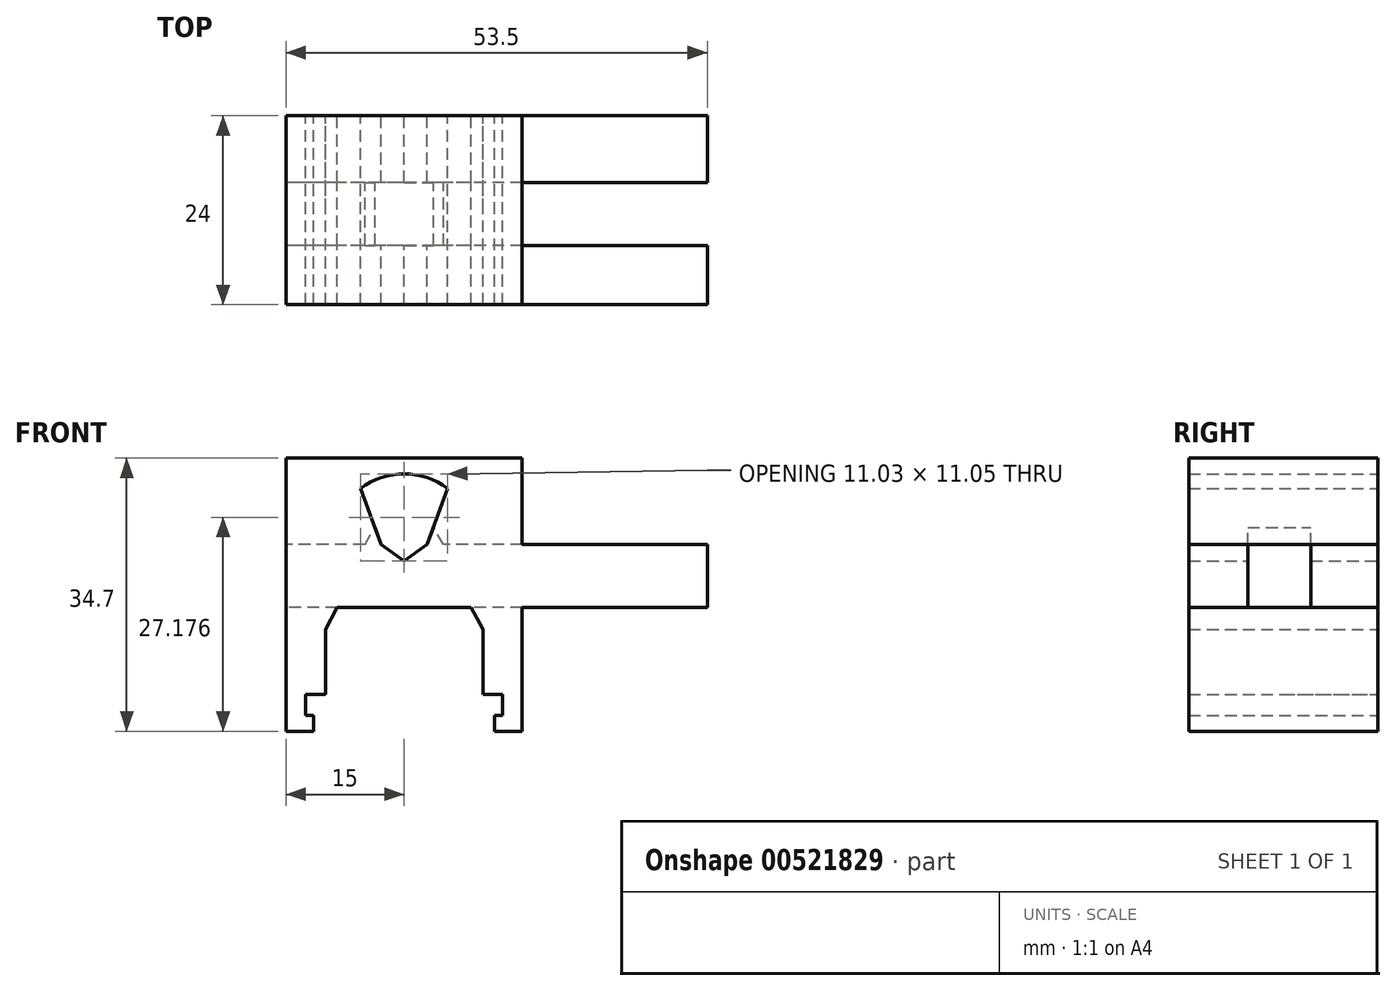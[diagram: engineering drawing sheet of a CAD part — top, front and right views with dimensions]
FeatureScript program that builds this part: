
annotation { "Feature Type Name" : "Feature", "Feature Type Description" : "" }
export const myFeature = defineFeature(function(context is Context, id is Id, definition is map)
    precondition{}
    {
        {
            var Q0;
            Q0=qCreatedBy(makeId("Front.planeOp"),FACE);
            var sketch = newSketch(context, id + "F0", { "sketchPlane" : qUnion([Q0])});
            skLineSegment(sketch, "E0.bottom", {"start": v(15, 15) * mm, "end": v(-15, 15) * mm});
            skLineSegment(sketch, "E0.top", {"start": v(15, -15) * mm, "end": v(-15, -15) * mm});
            skLineSegment(sketch, "E0.left", {"start": v(15, 15) * mm, "end": v(15, -15) * mm});
            skLineSegment(sketch, "E0.right", {"start": v(-15, 15) * mm, "end": v(-15, -15) * mm});
            skLineSegment(sketch, "E1", {"start": v(0, 0) * mm, "end": v(0, -17.35) * mm});
            skLineSegment(sketch, "E2.top", {"start": v(15, -19.7) * mm, "end": v(-15, -19.7) * mm});
            skLineSegment(sketch, "E2.left", {"start": v(15, -15) * mm, "end": v(15, -19.7) * mm});
            skLineSegment(sketch, "E2.right", {"start": v(-15, -15) * mm, "end": v(-15, -19.7) * mm});
            skPoint(sketch, "E2.middle", {"position": v(0, -17.35) * mm});
            skLineSegment(sketch, "E3.0", {"start": v(15, -17.7) * mm, "end": v(-15, -17.7) * mm});
            skLineSegment(sketch, "E4.0", {"start": v(-12.5, -15) * mm, "end": v(-12.5, -17.7) * mm});
            skLineSegment(sketch, "E5.0", {"start": v(12.5, -15) * mm, "end": v(12.5, -17.7) * mm});
            skLineSegment(sketch, "E6.0", {"start": v(-11.5, -17.7) * mm, "end": v(-11.5, -20) * mm});
            skLineSegment(sketch, "E7.0", {"start": v(11.5, -17.7) * mm, "end": v(11.5, -20) * mm});
            skCircle(sketch, "E8", {"center": v(0, 30) * mm, "radius": 2 * mm});
            skLineSegment(sketch, "E9", {"start": v(0, 30) * mm, "end": v(-5.14, 36.13) * mm});
            skPoint(sketch, "E9.endSnap0", {"position": v(0, 15) * mm});
            skLineSegment(sketch, "E10", {"start": v(0, 30) * mm, "end": v(9.64, 18.5) * mm});
            skLineSegment(sketch, "E11", {"start": v(0, 30) * mm, "end": v(-2.3, 28.07) * mm});
            skLineSegment(sketch, "E12", {"start": v(0, 30) * mm, "end": v(2.3, 31.93) * mm});
            skLineSegment(sketch, "E13", {"start": v(2.3, 31.93) * mm, "end": v(-5.14, 36.13) * mm});
            skLineSegment(sketch, "E14", {"start": v(-5.14, 36.13) * mm, "end": v(-2.3, 28.07) * mm});
            skLineSegment(sketch, "E15", {"start": v(9.64, 18.5) * mm, "end": v(-2.3, 28.07) * mm});
            skLineSegment(sketch, "E16", {"start": v(9.64, 18.5) * mm, "end": v(2.3, 31.93) * mm});
            skLineSegment(sketch, "E17", {"start": v(0, -15) * mm, "end": v(-10, -15) * mm});
            skLineSegment(sketch, "E18", {"start": v(0, -15) * mm, "end": v(10, -15) * mm});
            skLineSegment(sketch, "E19.bottom", {"start": v(8.5, 4) * mm, "end": v(-38.5, 4) * mm});
            skLineSegment(sketch, "E19.top", {"start": v(8.5, -4) * mm, "end": v(-38.5, -4) * mm});
            skLineSegment(sketch, "E19.left", {"start": v(8.5, 4) * mm, "end": v(8.5, -4) * mm});
            skLineSegment(sketch, "E19.right", {"start": v(-38.5, 4) * mm, "end": v(-38.5, -4) * mm});
            skPoint(sketch, "E19.middle", {"position": v(-15, 0) * mm});
            skLineSegment(sketch, "E20.bottom", {"start": v(38.5, 4) * mm, "end": v(-8.5, 4) * mm});
            skLineSegment(sketch, "E20.top", {"start": v(38.5, -4) * mm, "end": v(-8.5, -4) * mm});
            skLineSegment(sketch, "E20.left", {"start": v(38.5, 4) * mm, "end": v(38.5, -4) * mm});
            skLineSegment(sketch, "E20.right", {"start": v(-8.5, 4) * mm, "end": v(-8.5, -4) * mm});
            skPoint(sketch, "E20.middle", {"position": v(15, 0) * mm});
            skLineSegment(sketch, "E21", {"start": v(8.5, -4) * mm, "end": v(-2.93, 4) * mm});
            skLineSegment(sketch, "E22", {"start": v(-8.5, -4) * mm, "end": v(2.93, 4) * mm});
            skLineSegment(sketch, "E23", {"start": v(0, 0) * mm, "end": v(0, 45) * mm});
            skLineSegment(sketch, "E24", {"start": v(0, 0) * mm, "end": v(0, 30) * mm});
            skLineSegment(sketch, "E25.0", {"start": v(10, 15) * mm, "end": v(10, -15) * mm});
            skLineSegment(sketch, "E26.0", {"start": v(-10, 15.04) * mm, "end": v(-10, -15) * mm});
            skArc(sketch, "E27", {"start": v(5.51, 11.11) * mm, "mid": v(0, 13) * mm, "end": v(-5.51, 11.11) * mm});
            skLineSegment(sketch, "E28", {"start": v(2.93, 4) * mm, "end": v(5.51, 11.11) * mm});
            skLineSegment(sketch, "E29", {"start": v(-2.93, 4) * mm, "end": v(-5.51, 11.11) * mm});
            skLineSegment(sketch, "E30", {"start": v(8.5, -4) * mm, "end": v(10, -6.74) * mm});
            skLineSegment(sketch, "E31", {"start": v(-8.5, -4) * mm, "end": v(-10, -6.74) * mm});
            skLineSegment(sketch, "E32", {"start": v(5, 4) * mm, "end": v(3.73, 6.2) * mm});
            skLineSegment(sketch, "E33", {"start": v(-5, 4) * mm, "end": v(-3.73, 6.2) * mm});
            skSolve(sketch);
        }
        {
            var Q0;
            {var subQ0=sQuery(id+"F0.wireOp",EDGE,"E19.bottom");var subQ1=sQuery(id+"F0.wireOp",EDGE,"E0.right");var subQ2=makeQuery(id+"F0.imprint","INTERSECT",VERTEX,{"derivedFrom":[subQ1,subQ0]});Q0=makeQuery(id+"F0.imprint","IMPRINT",FACE,{"disambiguationData":[TD([[makeQuery(id+"F0.imprint","IMPRINT",EDGE,{"disambiguationData":[TD([[subQ2,-1.0]])],"derivedFrom":subQ1}),1.0]])]});}
            var Q1;
            {var subQ0=sQuery(id+"F0.wireOp",EDGE,"E0.left");var subQ1=sQuery(id+"F0.wireOp",EDGE,"E0.bottom");var subQ2=makeQuery(id+"F0.imprint","INTERSECT",VERTEX,{"derivedFrom":[subQ1,subQ0]});Q1=makeQuery(id+"F0.imprint","IMPRINT",FACE,{"disambiguationData":[TD([[makeQuery(id+"F0.imprint","IMPRINT",EDGE,{"disambiguationData":[TD([[subQ2,-1.0]])],"derivedFrom":subQ1}),1.0]])]});}
            var Q2;
            {var subQ7=sQuery(id+"F0.wireOp",EDGE,"E32");Q2=makeQuery(id+"F0.imprint","IMPRINT",FACE,{"disambiguationData":[TD([[makeQuery(id+"F0.imprint","IMPRINT",EDGE,{"derivedFrom":subQ7}),-1.0]])]});}
            var Q3;
            {var subQ0=sQuery(id+"F0.wireOp",EDGE,"E24");var subQ1=sQuery(id+"F0.wireOp",EDGE,"E1");var subQ2=makeQuery(id+"F0.imprint","INTERSECT",VERTEX,{"derivedFrom":[subQ1,subQ0]});Q3=makeQuery(id+"F0.imprint","IMPRINT",FACE,{"disambiguationData":[TD([[makeQuery(id+"F0.imprint","IMPRINT",EDGE,{"disambiguationData":[TD([[subQ2,-1.0]])],"derivedFrom":subQ1}),-1.0]])]});}
            var Q4;
            {var subQ4=sQuery(id+"F0.wireOp",EDGE,"E2.left");var subQ6=sQuery(id+"F0.wireOp",EDGE,"E2.top");var subQ7=makeQuery(id+"F0.imprint","INTERSECT",VERTEX,{"derivedFrom":[subQ6,subQ4]});Q4=makeQuery(id+"F0.imprint","IMPRINT",FACE,{"disambiguationData":[TD([[makeQuery(id+"F0.imprint","IMPRINT",EDGE,{"disambiguationData":[TD([[subQ7,-1.0]])],"derivedFrom":subQ6}),-1.0]])]});}
            var Q5;
            {var subQ0=sQuery(id+"F0.wireOp",EDGE,"E24");var subQ1=sQuery(id+"F0.wireOp",EDGE,"E1");var subQ2=makeQuery(id+"F0.imprint","INTERSECT",VERTEX,{"derivedFrom":[subQ1,subQ0]});Q5=makeQuery(id+"F0.imprint","IMPRINT",FACE,{"disambiguationData":[TD([[makeQuery(id+"F0.imprint","IMPRINT",EDGE,{"disambiguationData":[TD([[subQ2,-1.0]])],"derivedFrom":subQ1}),1.0]])]});}
            var Q6;
            {var subQ0=sQuery(id+"F0.wireOp",EDGE,"E30");Q6=makeQuery(id+"F0.imprint","IMPRINT",FACE,{"disambiguationData":[TD([[makeQuery(id+"F0.imprint","IMPRINT",EDGE,{"derivedFrom":subQ0}),1.0]])]});}
            var Q7;
            {var subQ3=sQuery(id+"F0.wireOp",EDGE,"E33");Q7=makeQuery(id+"F0.imprint","IMPRINT",FACE,{"disambiguationData":[TD([[makeQuery(id+"F0.imprint","IMPRINT",EDGE,{"derivedFrom":subQ3}),1.0]])]});}
            var Q8;
            {var subQ3=sQuery(id+"F0.wireOp",EDGE,"E5.0");Q8=makeQuery(id+"F0.imprint","IMPRINT",FACE,{"disambiguationData":[TD([[makeQuery(id+"F0.imprint","IMPRINT",EDGE,{"derivedFrom":subQ3}),1.0]])]});}
            var Q9;
            {var subQ5=sQuery(id+"F0.wireOp",EDGE,"E18");Q9=makeQuery(id+"F0.imprint","IMPRINT",FACE,{"disambiguationData":[TD([[makeQuery(id+"F0.imprint","IMPRINT",EDGE,{"derivedFrom":subQ5}),1.0]])]});}
            var Q10;
            {var subQ4=sQuery(id+"F0.wireOp",EDGE,"E20.top");var subQ5=sQuery(id+"F0.wireOp",EDGE,"E0.left");var subQ6=makeQuery(id+"F0.imprint","INTERSECT",VERTEX,{"derivedFrom":[subQ5,subQ4]});Q10=makeQuery(id+"F0.imprint","IMPRINT",FACE,{"disambiguationData":[TD([[makeQuery(id+"F0.imprint","IMPRINT",EDGE,{"disambiguationData":[TD([[subQ6,-1.0]])],"derivedFrom":subQ4}),1.0]])]});}
            var Q11;
            {var subQ5=sQuery(id+"F0.wireOp",EDGE,"E17");Q11=makeQuery(id+"F0.imprint","IMPRINT",FACE,{"disambiguationData":[TD([[makeQuery(id+"F0.imprint","IMPRINT",EDGE,{"derivedFrom":subQ5}),-1.0]])]});}
            var Q12;
            {var subQ1=sQuery(id+"F0.wireOp",EDGE,"E20.bottom");var subQ4=sQuery(id+"F0.wireOp",EDGE,"E24");var subQ5=makeQuery(id+"F0.imprint","INTERSECT",VERTEX,{"derivedFrom":[subQ1,subQ4]});Q12=makeQuery(id+"F0.imprint","IMPRINT",FACE,{"disambiguationData":[TD([[makeQuery(id+"F0.imprint","IMPRINT",EDGE,{"disambiguationData":[TD([[subQ5,-1.0]])],"derivedFrom":subQ4}),-1.0]])]});}
            var Q13;
            {var subQ1=sQuery(id+"F0.wireOp",EDGE,"E20.bottom");var subQ6=sQuery(id+"F0.wireOp",EDGE,"E24");var subQ8=makeQuery(id+"F0.imprint","INTERSECT",VERTEX,{"derivedFrom":[subQ1,subQ6]});Q13=makeQuery(id+"F0.imprint","IMPRINT",FACE,{"disambiguationData":[TD([[makeQuery(id+"F0.imprint","IMPRINT",EDGE,{"disambiguationData":[TD([[subQ8,-1.0]])],"derivedFrom":subQ6}),1.0]])]});}
            var Q14;
            {var subQ0=sQuery(id+"F0.wireOp",EDGE,"E20.bottom");var subQ1=sQuery(id+"F0.wireOp",EDGE,"E0.left");var subQ2=makeQuery(id+"F0.imprint","INTERSECT",VERTEX,{"derivedFrom":[subQ1,subQ0]});Q14=makeQuery(id+"F0.imprint","IMPRINT",FACE,{"disambiguationData":[TD([[makeQuery(id+"F0.imprint","IMPRINT",EDGE,{"disambiguationData":[TD([[subQ2,-1.0]])],"derivedFrom":subQ1}),-1.0]])]});}
            var Q15;
            {var subQ4=sQuery(id+"F0.wireOp",EDGE,"E2.right");var subQ6=sQuery(id+"F0.wireOp",EDGE,"E2.top");var subQ7=makeQuery(id+"F0.imprint","INTERSECT",VERTEX,{"derivedFrom":[subQ6,subQ4]});Q15=makeQuery(id+"F0.imprint","IMPRINT",FACE,{"disambiguationData":[TD([[makeQuery(id+"F0.imprint","IMPRINT",EDGE,{"disambiguationData":[TD([[subQ7,1.0]])],"derivedFrom":subQ6}),-1.0]])]});}
            var Q16;
            {var subQ0=sQuery(id+"F0.wireOp",EDGE,"E19.left");Q16=makeQuery(id+"F0.imprint","IMPRINT",FACE,{"disambiguationData":[TD([[makeQuery(id+"F0.imprint","IMPRINT",EDGE,{"derivedFrom":subQ0}),1.0]])]});}
            var Q17;
            {var subQ3=sQuery(id+"F0.wireOp",EDGE,"E33");Q17=makeQuery(id+"F0.imprint","IMPRINT",FACE,{"disambiguationData":[TD([[makeQuery(id+"F0.imprint","IMPRINT",EDGE,{"derivedFrom":subQ3}),-1.0]])]});}
            var Q18;
            {var subQ3=sQuery(id+"F0.wireOp",EDGE,"E4.0");Q18=makeQuery(id+"F0.imprint","IMPRINT",FACE,{"disambiguationData":[TD([[makeQuery(id+"F0.imprint","IMPRINT",EDGE,{"derivedFrom":subQ3}),-1.0]])]});}
            var Q19;
            {var subQ0=sQuery(id+"F0.wireOp",EDGE,"E0.right");var subQ1=sQuery(id+"F0.wireOp",EDGE,"E0.bottom");var subQ2=makeQuery(id+"F0.imprint","INTERSECT",VERTEX,{"derivedFrom":[subQ1,subQ0]});Q19=makeQuery(id+"F0.imprint","IMPRINT",FACE,{"disambiguationData":[TD([[makeQuery(id+"F0.imprint","IMPRINT",EDGE,{"disambiguationData":[TD([[subQ2,1.0]])],"derivedFrom":subQ1}),1.0]])]});}
            var Q20;
            {var subQ0=sQuery(id+"F0.wireOp",EDGE,"E31");Q20=makeQuery(id+"F0.imprint","IMPRINT",FACE,{"disambiguationData":[TD([[makeQuery(id+"F0.imprint","IMPRINT",EDGE,{"derivedFrom":subQ0}),-1.0]])]});}
            var Q21;
            {var subQ1=sQuery(id+"F0.wireOp",EDGE,"E19.left");Q21=makeQuery(id+"F0.imprint","IMPRINT",FACE,{"disambiguationData":[TD([[makeQuery(id+"F0.imprint","IMPRINT",EDGE,{"derivedFrom":subQ1}),-1.0]])]});}
            var Q22;
            {var subQ0=sQuery(id+"F0.wireOp",EDGE,"E20.right");Q22=makeQuery(id+"F0.imprint","IMPRINT",FACE,{"disambiguationData":[TD([[makeQuery(id+"F0.imprint","IMPRINT",EDGE,{"derivedFrom":subQ0}),1.0]])]});}
            var Q23;
            {var subQ3=sQuery(id+"F0.wireOp",EDGE,"E32");Q23=makeQuery(id+"F0.imprint","IMPRINT",FACE,{"disambiguationData":[TD([[makeQuery(id+"F0.imprint","IMPRINT",EDGE,{"derivedFrom":subQ3}),1.0]])]});}
            var Q24;
            {var subQ1=sQuery(id+"F0.wireOp",EDGE,"E20.bottom");var subQ3=sQuery(id+"F0.wireOp",EDGE,"E24");var subQ4=makeQuery(id+"F0.imprint","INTERSECT",VERTEX,{"derivedFrom":[subQ1,subQ3]});Q24=makeQuery(id+"F0.imprint","IMPRINT",FACE,{"disambiguationData":[TD([[makeQuery(id+"F0.imprint","IMPRINT",EDGE,{"disambiguationData":[TD([[subQ4,1.0]])],"derivedFrom":subQ1}),1.0]])]});}
            var Q25;
            {var subQ1=sQuery(id+"F0.wireOp",EDGE,"E20.bottom");var subQ3=sQuery(id+"F0.wireOp",EDGE,"E24");var subQ4=makeQuery(id+"F0.imprint","INTERSECT",VERTEX,{"derivedFrom":[subQ1,subQ3]});Q25=makeQuery(id+"F0.imprint","IMPRINT",FACE,{"disambiguationData":[TD([[makeQuery(id+"F0.imprint","IMPRINT",EDGE,{"disambiguationData":[TD([[subQ4,-1.0]])],"derivedFrom":subQ1}),1.0]])]});}
            var Q26;
            {var subQ0=sQuery(id+"F0.wireOp",EDGE,"E20.right");Q26=makeQuery(id+"F0.imprint","IMPRINT",FACE,{"disambiguationData":[TD([[makeQuery(id+"F0.imprint","IMPRINT",EDGE,{"derivedFrom":subQ0}),-1.0]])]});}
            var Q27;
            {var subQ0=sQuery(id+"F0.wireOp",EDGE,"E19.top");var subQ1=sQuery(id+"F0.wireOp",EDGE,"E0.right");var subQ2=makeQuery(id+"F0.imprint","INTERSECT",VERTEX,{"derivedFrom":[subQ1,subQ0]});Q27=makeQuery(id+"F0.imprint","IMPRINT",FACE,{"disambiguationData":[TD([[makeQuery(id+"F0.imprint","IMPRINT",EDGE,{"disambiguationData":[TD([[subQ2,1.0]])],"derivedFrom":subQ0}),1.0]])]});}
            extrude(context, id + "F1", {"entities" : qUnion([Q0, Q1, Q2, Q3, Q4, Q5, Q6, Q7, Q8, Q9, Q10, Q11, Q12, Q13, Q14, Q15, Q16, Q17, Q18, Q19, Q20, Q21, Q22, Q23, Q24, Q25, Q26, Q27]), "depth" : 24 * mm, "offsetDistance" : 25 * mm});
        }
        {
            var Q0;
            Q0=makeQuery(id+"F1.opExtrude","SWEPT_FACE",FACE,{"disambiguationData":[OSD([sQuery(id+"F0.wireOp",EDGE,"E0.top"),sQuery(id+"F0.wireOp",EDGE,"E17"),sQuery(id+"F0.wireOp",EDGE,"E18")])]});
            var sketch = newSketch(context, id + "F2", { "sketchPlane" : qUnion([Q0])});
            skLineSegment(sketch, "E34", {"start": v(0, 0) * mm, "end": v(0, 12) * mm});
            skPoint(sketch, "E34.endSnap0", {"position": v(0, 0) * mm});
            skCircle(sketch, "E35", {"center": v(0, 12) * mm, "radius": 10 * mm});
            skLineSegment(sketch, "E36", {"start": v(0, 12) * mm, "end": v(0, 22) * mm});
            skSolve(sketch);
        }
        {
            var Q0;
            {var subQ0=sQuery(id+"F2.wireOp",EDGE,"E36");Q0=makeQuery(id+"F2.imprint","IMPRINT",FACE,{"disambiguationData":[TD([[makeQuery(id+"F2.imprint","IMPRINT",EDGE,{"derivedFrom":subQ0}),1.0]])]});}
            var Q1;
            Q1=sQuery(id+"F2.wireOp",EDGE,"E34");
            revolve(context, id + "F3", {"operationType" : NewBodyOperationType.REMOVE, "entities" : qUnion([Q0]), "axis" : qUnion([Q1]), "revolveType" : RevolveType.FULL, "oppositeDirection" : true});
        }
        {
            var Q0;
            {var subQ5=sQuery(id+"F0.wireOp",EDGE,"E18");Q0=makeQuery(id+"F0.imprint","IMPRINT",FACE,{"disambiguationData":[TD([[makeQuery(id+"F0.imprint","IMPRINT",EDGE,{"derivedFrom":subQ5}),1.0]])]});}
            var Q1;
            {var subQ0=sQuery(id+"F0.wireOp",EDGE,"E24");var subQ1=sQuery(id+"F0.wireOp",EDGE,"E1");var subQ2=makeQuery(id+"F0.imprint","INTERSECT",VERTEX,{"derivedFrom":[subQ1,subQ0]});Q1=makeQuery(id+"F0.imprint","IMPRINT",FACE,{"disambiguationData":[TD([[makeQuery(id+"F0.imprint","IMPRINT",EDGE,{"disambiguationData":[TD([[subQ2,-1.0]])],"derivedFrom":subQ1}),1.0]])]});}
            var Q2;
            {var subQ1=sQuery(id+"F0.wireOp",EDGE,"E19.left");Q2=makeQuery(id+"F0.imprint","IMPRINT",FACE,{"disambiguationData":[TD([[makeQuery(id+"F0.imprint","IMPRINT",EDGE,{"derivedFrom":subQ1}),-1.0]])]});}
            var Q3;
            {var subQ1=sQuery(id+"F0.wireOp",EDGE,"E20.bottom");var subQ3=sQuery(id+"F0.wireOp",EDGE,"E24");var subQ4=makeQuery(id+"F0.imprint","INTERSECT",VERTEX,{"derivedFrom":[subQ1,subQ3]});Q3=makeQuery(id+"F0.imprint","IMPRINT",FACE,{"disambiguationData":[TD([[makeQuery(id+"F0.imprint","IMPRINT",EDGE,{"disambiguationData":[TD([[subQ4,1.0]])],"derivedFrom":subQ1}),1.0]])]});}
            var Q4;
            {var subQ1=sQuery(id+"F0.wireOp",EDGE,"E20.bottom");var subQ3=sQuery(id+"F0.wireOp",EDGE,"E24");var subQ4=makeQuery(id+"F0.imprint","INTERSECT",VERTEX,{"derivedFrom":[subQ1,subQ3]});Q4=makeQuery(id+"F0.imprint","IMPRINT",FACE,{"disambiguationData":[TD([[makeQuery(id+"F0.imprint","IMPRINT",EDGE,{"disambiguationData":[TD([[subQ4,-1.0]])],"derivedFrom":subQ1}),1.0]])]});}
            var Q5;
            {var subQ0=sQuery(id+"F0.wireOp",EDGE,"E24");var subQ1=sQuery(id+"F0.wireOp",EDGE,"E1");var subQ2=makeQuery(id+"F0.imprint","INTERSECT",VERTEX,{"derivedFrom":[subQ1,subQ0]});Q5=makeQuery(id+"F0.imprint","IMPRINT",FACE,{"disambiguationData":[TD([[makeQuery(id+"F0.imprint","IMPRINT",EDGE,{"disambiguationData":[TD([[subQ2,-1.0]])],"derivedFrom":subQ1}),-1.0]])]});}
            var Q6;
            {var subQ0=sQuery(id+"F0.wireOp",EDGE,"E20.right");Q6=makeQuery(id+"F0.imprint","IMPRINT",FACE,{"disambiguationData":[TD([[makeQuery(id+"F0.imprint","IMPRINT",EDGE,{"derivedFrom":subQ0}),1.0]])]});}
            var Q7;
            {var subQ0=sQuery(id+"F0.wireOp",EDGE,"E20.right");Q7=makeQuery(id+"F0.imprint","IMPRINT",FACE,{"disambiguationData":[TD([[makeQuery(id+"F0.imprint","IMPRINT",EDGE,{"derivedFrom":subQ0}),-1.0]])]});}
            var Q8;
            {var subQ0=sQuery(id+"F0.wireOp",EDGE,"E19.bottom");var subQ1=sQuery(id+"F0.wireOp",EDGE,"E0.right");var subQ2=makeQuery(id+"F0.imprint","INTERSECT",VERTEX,{"derivedFrom":[subQ1,subQ0]});Q8=makeQuery(id+"F0.imprint","IMPRINT",FACE,{"disambiguationData":[TD([[makeQuery(id+"F0.imprint","IMPRINT",EDGE,{"disambiguationData":[TD([[subQ2,-1.0]])],"derivedFrom":subQ1}),1.0]])]});}
            var Q9;
            {var subQ0=sQuery(id+"F0.wireOp",EDGE,"E19.left");Q9=makeQuery(id+"F0.imprint","IMPRINT",FACE,{"disambiguationData":[TD([[makeQuery(id+"F0.imprint","IMPRINT",EDGE,{"derivedFrom":subQ0}),1.0]])]});}
            var Q10;
            {var subQ0=sQuery(id+"F0.wireOp",EDGE,"E20.bottom");var subQ1=sQuery(id+"F0.wireOp",EDGE,"E0.left");var subQ2=makeQuery(id+"F0.imprint","INTERSECT",VERTEX,{"derivedFrom":[subQ1,subQ0]});Q10=makeQuery(id+"F0.imprint","IMPRINT",FACE,{"disambiguationData":[TD([[makeQuery(id+"F0.imprint","IMPRINT",EDGE,{"disambiguationData":[TD([[subQ2,-1.0]])],"derivedFrom":subQ1}),-1.0]])]});}
            var Q11;
            {var subQ1=sQuery(id+"F0.wireOp",EDGE,"E20.bottom");var subQ4=sQuery(id+"F0.wireOp",EDGE,"E24");var subQ5=makeQuery(id+"F0.imprint","INTERSECT",VERTEX,{"derivedFrom":[subQ1,subQ4]});Q11=makeQuery(id+"F0.imprint","IMPRINT",FACE,{"disambiguationData":[TD([[makeQuery(id+"F0.imprint","IMPRINT",EDGE,{"disambiguationData":[TD([[subQ5,-1.0]])],"derivedFrom":subQ4}),-1.0]])]});}
            var Q12;
            {var subQ1=sQuery(id+"F0.wireOp",EDGE,"E20.bottom");var subQ4=sQuery(id+"F0.wireOp",EDGE,"E24");var subQ5=makeQuery(id+"F0.imprint","INTERSECT",VERTEX,{"derivedFrom":[subQ1,subQ4]});Q12=makeQuery(id+"F0.imprint","IMPRINT",FACE,{"disambiguationData":[TD([[makeQuery(id+"F0.imprint","IMPRINT",EDGE,{"disambiguationData":[TD([[subQ5,-1.0]])],"derivedFrom":subQ4}),1.0]])]});}
            var Q13;
            {var subQ5=sQuery(id+"F0.wireOp",EDGE,"E17");Q13=makeQuery(id+"F0.imprint","IMPRINT",FACE,{"disambiguationData":[TD([[makeQuery(id+"F0.imprint","IMPRINT",EDGE,{"derivedFrom":subQ5}),-1.0]])]});}
            var Q14;
            {var subQ3=sQuery(id+"F0.wireOp",EDGE,"E32");Q14=makeQuery(id+"F0.imprint","IMPRINT",FACE,{"disambiguationData":[TD([[makeQuery(id+"F0.imprint","IMPRINT",EDGE,{"derivedFrom":subQ3}),1.0]])]});}
            var Q15;
            {var subQ3=sQuery(id+"F0.wireOp",EDGE,"E33");Q15=makeQuery(id+"F0.imprint","IMPRINT",FACE,{"disambiguationData":[TD([[makeQuery(id+"F0.imprint","IMPRINT",EDGE,{"derivedFrom":subQ3}),-1.0]])]});}
            extrude(context, id + "F4", {"entities" : qUnion([Q0, Q1, Q2, Q3, Q4, Q5, Q6, Q7, Q8, Q9, Q10, Q11, Q12, Q13, Q14, Q15]), "operationType" : NewBodyOperationType.REMOVE, "depth" : 16.5 * mm, "offsetDistance" : 25 * mm, "hasSecondDirection" : true, "secondDirectionOppositeDirection" : false, "secondDirectionDepth" : 8.5 * mm});
        }
        {
            var Q0;
            Q0=makeQuery(id+"F1.opExtrude","CAP_FACE",FACE,{"disambiguationData":[OSD([sQuery(id+"F0.wireOp",EDGE,"E0.bottom"),sQuery(id+"F0.wireOp",EDGE,"E0.left"),sQuery(id+"F0.wireOp",EDGE,"E0.right"),sQuery(id+"F0.wireOp",EDGE,"E0.top"),sQuery(id+"F0.wireOp",EDGE,"E2.top"),sQuery(id+"F0.wireOp",EDGE,"E2.left"),sQuery(id+"F0.wireOp",EDGE,"E2.right"),sQuery(id+"F0.wireOp",EDGE,"E3.0"),sQuery(id+"F0.wireOp",EDGE,"E4.0"),sQuery(id+"F0.wireOp",EDGE,"E5.0"),sQuery(id+"F0.wireOp",EDGE,"E6.0"),sQuery(id+"F0.wireOp",EDGE,"E7.0"),sQuery(id+"F0.wireOp",EDGE,"E17"),sQuery(id+"F0.wireOp",EDGE,"E18")])],"isStart":true});
            var sketch = newSketch(context, id + "F5", { "sketchPlane" : qUnion([Q0])});
            skCircle(sketch, "E37", {"center": v(0, 5) * mm, "radius": 2 * mm});
            skLineSegment(sketch, "E38", {"start": v(0, 5) * mm, "end": v(0, 0) * mm});
            skSolve(sketch);
        }
        {
            var Q0;
            Q0=makeQuery(id+"F5.imprint","IMPRINT",FACE,{"disambiguationData":[TD([[makeQuery(id+"F5.imprint","IMPRINT",EDGE,{"derivedFrom":sQuery(id+"F5.wireOp",EDGE,"E37")}),1.0]])]});
            extrude(context, id + "F6", {"entities" : qUnion([Q0]), "operationType" : NewBodyOperationType.REMOVE, "oppositeDirection" : true, "depth" : 21 * mm, "offsetDistance" : 25 * mm, "hasSecondDirection" : true, "secondDirectionOppositeDirection" : true, "secondDirectionDepth" : 4 * mm});
        }
    });
